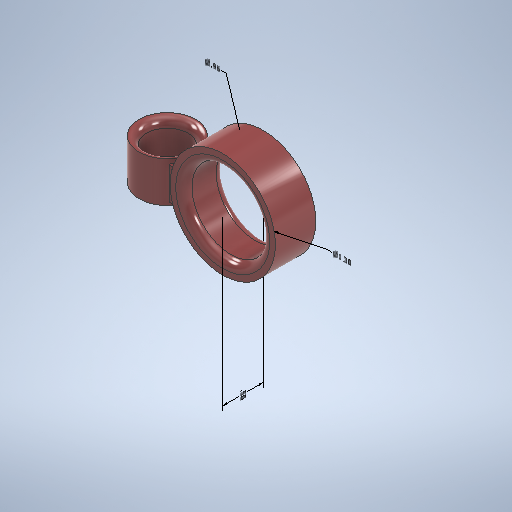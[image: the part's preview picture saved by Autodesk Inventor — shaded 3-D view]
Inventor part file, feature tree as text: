
AUTODESK INVENTOR PART (.ipt)
format: ipt  version: 2025.2 (Build 292293000, 293)  size: 362,496 bytes
history: native  units: in
note: dims shown in document units (in); Inventor stores cm internally (conversion verified against a paired STEP export)
features: other x4, sketch x4, extrude x3, plane x2, fillet x1
ambient origin geometry x8: Origin, YZ Plane, XZ Plane, XY Plane, X Axis, Y Axis, Z Axis, Center Point
bodies: Solid1 (feature_tree)
feature tree (14):
  other  "Annotations"
  extrude  "Extrusion1"  Depth=0.7in
  plane  "Work Plane1"
  sketch  "Sketch2"  dims[d2=0.5in d3=0.0in d4=1.0in d5=0.35in]
  plane  "Work Plane3"
  extrude  "Extrusion2"  Depth=0.35in
  fillet  "Fillet1"  Radius=0.35in
  extrude  "Extrusion3"  Depth=0.5in
  sketch  "Sketch1"  dims[d0=0.51in d1=0.7in]
  sketch  "Sketch5"  dims[d6=0.5in d7=0.5in]
  sketch  "Sketch6"  dims[d8=90.0deg d10=0.96in d11=0.25in d12=1.3in d13=0.5in d14=0.0in d15=0.1in d16=0.4in d17=0.0in d18=1.9754in d19=0.96in d20=0.5in d21=0.0811in d22=1.3in]
  other  "Diameter Dimension 1"
  other  "Linear Dimension 1"
  other  "Diameter Dimension 2"
